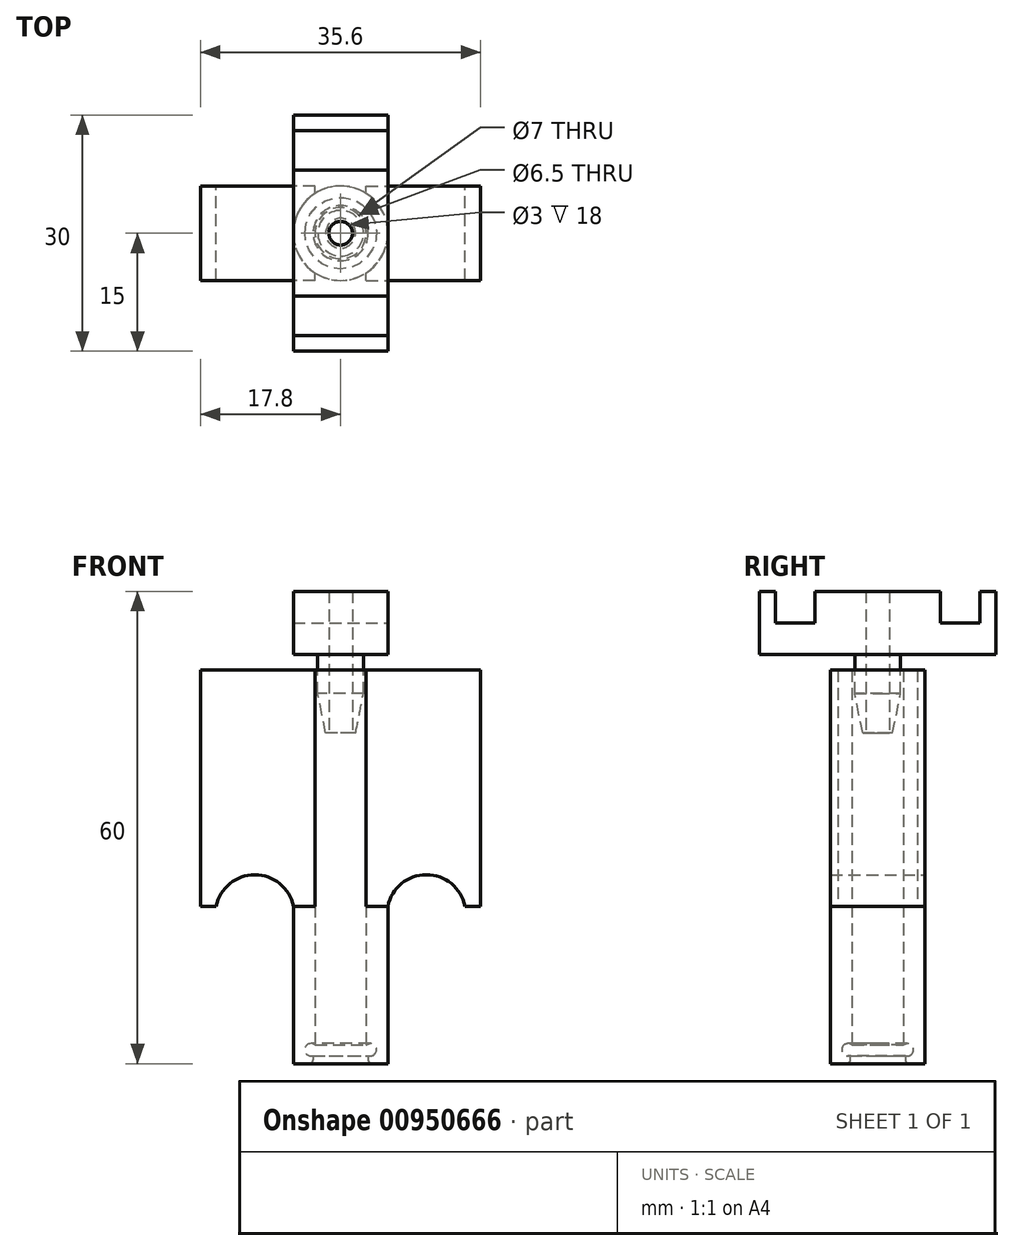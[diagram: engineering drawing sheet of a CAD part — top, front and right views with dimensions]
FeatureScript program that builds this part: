
annotation { "Feature Type Name" : "Feature", "Feature Type Description" : "" }
export const myFeature = defineFeature(function(context is Context, id is Id, definition is map)
    precondition{}
    {
        {
            var Q0;
            Q0=qCreatedBy(makeId("Front.planeOp"),FACE);
            var sketch = newSketch(context, id + "F0", { "sketchPlane" : qUnion([Q0])});
            skLineSegment(sketch, "E0.bottom", {"start": v(-3.5, 0) * mm, "end": v(-6, 0) * mm});
            skLineSegment(sketch, "E0.top", {"start": v(-3.25, 50) * mm, "end": v(-6, 50) * mm});
            skLineSegment(sketch, "E0.left", {"start": v(-3.25, 2.38) * mm, "end": v(-3.25, 50) * mm});
            skLineSegment(sketch, "E0.right", {"start": v(-6, 0) * mm, "end": v(-6, 50) * mm});
            skArc(sketch, "E1", {"start": v(-3.25, 2.38) * mm, "mid": v(-4.54, 1.9) * mm, "end": v(-3.5, 1) * mm});
            skLineSegment(sketch, "E2", {"start": v(0, 0) * mm, "end": v(0, 57.31) * mm, "construction": true});
            skLineSegment(sketch, "E3", {"start": v(-3.5, 1) * mm, "end": v(-3.5, 0) * mm});
            skSolve(sketch);
        }
        {
            var Q0;
            {var subQ3=sQuery(id+"F0.wireOp",EDGE,"E0.bottom");Q0=makeQuery(id+"F0.imprint","IMPRINT",FACE,{"disambiguationData":[TD([[makeQuery(id+"F0.imprint","IMPRINT",EDGE,{"derivedFrom":subQ3}),-1.0]])]});}
            var Q1;
            Q1=sQuery(id+"F0.wireOp",EDGE,"E2");
            revolve(context, id + "F1", {"surfaceOperationType" : NewSurfaceOperationType.NEW, "entities" : qUnion([Q0]), "axis" : qUnion([Q1]), "revolveType" : RevolveType.FULL});
        }
        {
            var Q0;
            Q0=qCreatedBy(makeId("Front.planeOp"),FACE);
            var sketch = newSketch(context, id + "F2", { "sketchPlane" : qUnion([Q0])});
            skLineSegment(sketch, "E4.0", {"start": v(6, 50) * mm, "end": v(-6, 50) * mm});
            skLineSegment(sketch, "E5", {"start": v(-3.25, 2.6) * mm, "end": v(-3.25, 50) * mm});
            skLineSegment(sketch, "E6", {"start": v(3.25, 50) * mm, "end": v(3.25, 2.6) * mm});
            skLineSegment(sketch, "E7.bottom", {"start": v(-3.25, 50) * mm, "end": v(-17.8, 50) * mm});
            skLineSegment(sketch, "E7.top", {"start": v(-3.25, 20) * mm, "end": v(-17.8, 20) * mm});
            skLineSegment(sketch, "E7.left", {"start": v(-3.25, 50) * mm, "end": v(-3.25, 20) * mm});
            skLineSegment(sketch, "E7.right", {"start": v(-17.8, 50) * mm, "end": v(-17.8, 20) * mm});
            skLineSegment(sketch, "E8.bottom", {"start": v(3.25, 50) * mm, "end": v(17.8, 50) * mm});
            skLineSegment(sketch, "E8.top", {"start": v(3.25, 20) * mm, "end": v(17.8, 20) * mm});
            skLineSegment(sketch, "E8.left", {"start": v(3.25, 50) * mm, "end": v(3.25, 20) * mm});
            skLineSegment(sketch, "E8.right", {"start": v(17.8, 50) * mm, "end": v(17.8, 20) * mm});
            skArc(sketch, "E9", {"start": v(-6, 20) * mm, "mid": v(-10.9, 24) * mm, "end": v(-15.8, 20) * mm});
            skLineSegment(sketch, "E10", {"start": v(-6, 0) * mm, "end": v(-6, 50) * mm});
            skLineSegment(sketch, "E11", {"start": v(6, 50) * mm, "end": v(6, 0) * mm});
            skArc(sketch, "E12.MirrorCS", {"start": v(6, 20) * mm, "mid": v(10.9, 24) * mm, "end": v(15.8, 20) * mm});
            skSolve(sketch);
        }
        {
            var Q0;
            {var subQ3=sQuery(id+"F2.wireOp",EDGE,"E7.bottom");Q0=makeQuery(id+"F2.imprint","IMPRINT",FACE,{"disambiguationData":[TD([[makeQuery(id+"F2.imprint","IMPRINT",EDGE,{"derivedFrom":subQ3}),1.0]])]});}
            var Q1;
            {var subQ1=sQuery(id+"F2.wireOp",EDGE,"E8.bottom");Q1=makeQuery(id+"F2.imprint","IMPRINT",FACE,{"disambiguationData":[TD([[makeQuery(id+"F2.imprint","IMPRINT",EDGE,{"derivedFrom":subQ1}),-1.0]])]});}
            var Q2;
            {var subQ0=sQuery(id+"F2.wireOp",EDGE,"E6");var subQ1=sQuery(id+"F2.wireOp",EDGE,"E4.0");var subQ2=makeQuery(id+"F2.imprint","INTERSECT",VERTEX,{"derivedFrom":[subQ1,subQ0]});Q2=makeQuery(id+"F2.imprint","IMPRINT",FACE,{"disambiguationData":[TD([[makeQuery(id+"F2.imprint","IMPRINT",EDGE,{"disambiguationData":[TD([[subQ2,-1.0]])],"derivedFrom":subQ0}),1.0]])]});}
            var Q3;
            {var subQ3=sQuery(id+"F2.wireOp",EDGE,"E5");var subQ5=sQuery(id+"F2.wireOp",EDGE,"E7.top");var subQ7=makeQuery(id+"F2.imprint","INTERSECT",VERTEX,{"derivedFrom":[subQ3,subQ5]});Q3=makeQuery(id+"F2.imprint","IMPRINT",FACE,{"disambiguationData":[TD([[makeQuery(id+"F2.imprint","IMPRINT",EDGE,{"disambiguationData":[TD([[subQ7,-1.0]])],"derivedFrom":subQ3}),1.0]])]});}
            extrude(context, id + "F3", {"entities" : qUnion([Q0, Q1, Q2, Q3]), "operationType" : NewBodyOperationType.ADD, "endBound" : BoundingType.SYMMETRIC, "depth" : 12 * mm, "offsetDistance" : 25 * mm});
        }
        {
            var Q0;
            {var subQ0=sQuery(id+"F2.wireOp",EDGE,"E4.0");Q0=makeQuery(id+"F3.boolean.opBoolean","MERGE",FACE,{"derivedFrom":[makeQuery(id+"F1.opRevolve","SWEPT_FACE",FACE,{"disambiguationData":[OSD([sQuery(id+"F0.wireOp",EDGE,"E0.top")])]}),makeQuery(id+"F3.opExtrude","SWEPT_FACE",FACE,{"disambiguationData":[OSD([subQ0,sQuery(id+"F2.wireOp",EDGE,"E7.bottom")])]}),makeQuery(id+"F3.opExtrude","SWEPT_FACE",FACE,{"disambiguationData":[OSD([subQ0,sQuery(id+"F2.wireOp",EDGE,"E8.bottom")])]})]});}
            cPlane(context, id + "F4", {"entities" : qUnion([Q0]), "cplaneType" : CPlaneType.OFFSET, "offset" : 2 * mm, "width" : 150 * mm, "height" : 150 * mm});
        }
        {
            var Q0;
            Q0=qCreatedBy(id+"F4.planeOp",FACE);
            var sketch = newSketch(context, id + "F5", { "sketchPlane" : qUnion([Q0])});
            skLineSegment(sketch, "E13.bottom", {"start": v(-6, 15) * mm, "end": v(6, 15) * mm});
            skLineSegment(sketch, "E13.top", {"start": v(-6, -15) * mm, "end": v(6, -15) * mm});
            skLineSegment(sketch, "E13.left", {"start": v(-6, 15) * mm, "end": v(-6, -15) * mm});
            skLineSegment(sketch, "E13.right", {"start": v(6, 15) * mm, "end": v(6, -15) * mm});
            skPoint(sketch, "E13.middle", {"position": v(0, 0) * mm});
            skCircle(sketch, "E14", {"center": v(0, 0) * mm, "radius": 1.5 * mm});
            skLineSegment(sketch, "E15", {"start": v(-6, 13) * mm, "end": v(6, 13) * mm});
            skLineSegment(sketch, "E16", {"start": v(-6, 8) * mm, "end": v(6, 8) * mm});
            skLineSegment(sketch, "E17.MirrorCS", {"start": v(-6, -13) * mm, "end": v(6, -13) * mm});
            skLineSegment(sketch, "E18.MirrorCS", {"start": v(-6, -8) * mm, "end": v(6, -8) * mm});
            skCircle(sketch, "E19", {"center": v(0, 0) * mm, "radius": 2.9 * mm});
            skSolve(sketch);
        }
        {
            var Q0;
            Q0=makeQuery(id+"F5.imprint","IMPRINT",FACE,{"disambiguationData":[TD([[makeQuery(id+"F5.imprint","IMPRINT",EDGE,{"derivedFrom":sQuery(id+"F5.wireOp",EDGE,"E14")}),-1.0]])]});
            var Q1;
            {var subQ0=sQuery(id+"F5.wireOp",EDGE,"E13.top");Q1=makeQuery(id+"F5.imprint","IMPRINT",FACE,{"disambiguationData":[TD([[makeQuery(id+"F5.imprint","IMPRINT",EDGE,{"derivedFrom":subQ0}),1.0]])]});}
            var Q2;
            {var subQ0=sQuery(id+"F5.wireOp",EDGE,"E13.bottom");Q2=makeQuery(id+"F5.imprint","IMPRINT",FACE,{"disambiguationData":[TD([[makeQuery(id+"F5.imprint","IMPRINT",EDGE,{"derivedFrom":subQ0}),-1.0]])]});}
            var Q3;
            {var subQ1=sQuery(id+"F5.wireOp",EDGE,"E16");Q3=makeQuery(id+"F5.imprint","IMPRINT",FACE,{"disambiguationData":[TD([[makeQuery(id+"F5.imprint","IMPRINT",EDGE,{"derivedFrom":subQ1}),-1.0]])]});}
            extrude(context, id + "F6", {"entities" : qUnion([Q0, Q1, Q2, Q3]), "depth" : 8 * mm, "offsetDistance" : 25 * mm});
        }
        {
            var Q0;
            {var subQ0=sQuery(id+"F5.wireOp",EDGE,"E15");Q0=makeQuery(id+"F5.imprint","IMPRINT",FACE,{"disambiguationData":[TD([[makeQuery(id+"F5.imprint","IMPRINT",EDGE,{"derivedFrom":subQ0}),-1.0]])]});}
            var Q1;
            {var subQ0=sQuery(id+"F5.wireOp",EDGE,"E17.MirrorCS");Q1=makeQuery(id+"F5.imprint","IMPRINT",FACE,{"disambiguationData":[TD([[makeQuery(id+"F5.imprint","IMPRINT",EDGE,{"derivedFrom":subQ0}),1.0]])]});}
            extrude(context, id + "F7", {"entities" : qUnion([Q0, Q1]), "operationType" : NewBodyOperationType.ADD, "depth" : 4 * mm, "offsetDistance" : 25 * mm});
        }
        {
            var Q0;
            Q0=makeQuery(id+"F5.imprint","IMPRINT",FACE,{"disambiguationData":[TD([[makeQuery(id+"F5.imprint","IMPRINT",EDGE,{"derivedFrom":sQuery(id+"F5.wireOp",EDGE,"E14")}),-1.0]])]});
            extrude(context, id + "F8", {"entities" : qUnion([Q0]), "operationType" : NewBodyOperationType.ADD, "oppositeDirection" : true, "depth" : 10 * mm, "offsetDistance" : 25 * mm});
        }
        {
            var Q0;
            Q0=makeQuery(id+"F8.opExtrude","CAP_EDGE",EDGE,{"disambiguationData":[OSD([sQuery(id+"F5.wireOp",EDGE,"E19")])],"isStart":false});
            chamfer(context, id + "F9", {"entities" : qUnion([Q0]), "chamferType" : ChamferType.TWO_OFFSETS, "width1" : 5 * mm, "oppositeDirection" : false, "width2" : 1 * mm, "tangentPropagation" : true});
        }
        {
            var Q0;
            Q0=makeQuery(id+"F1.opRevolve","SWEPT_EDGE",EDGE,{"disambiguationData":[OSD([sQuery(id+"F0.wireOp",EDGE,"E0.bottom"),sQuery(id+"F0.wireOp",EDGE,"E3")])]});
            fillet(context, id + "F10", {"entities" : qUnion([Q0]), "radius" : 0.5 * mm, "tangentPropagation" : true, "allowEdgeOverflow" : false});
        }
    });
